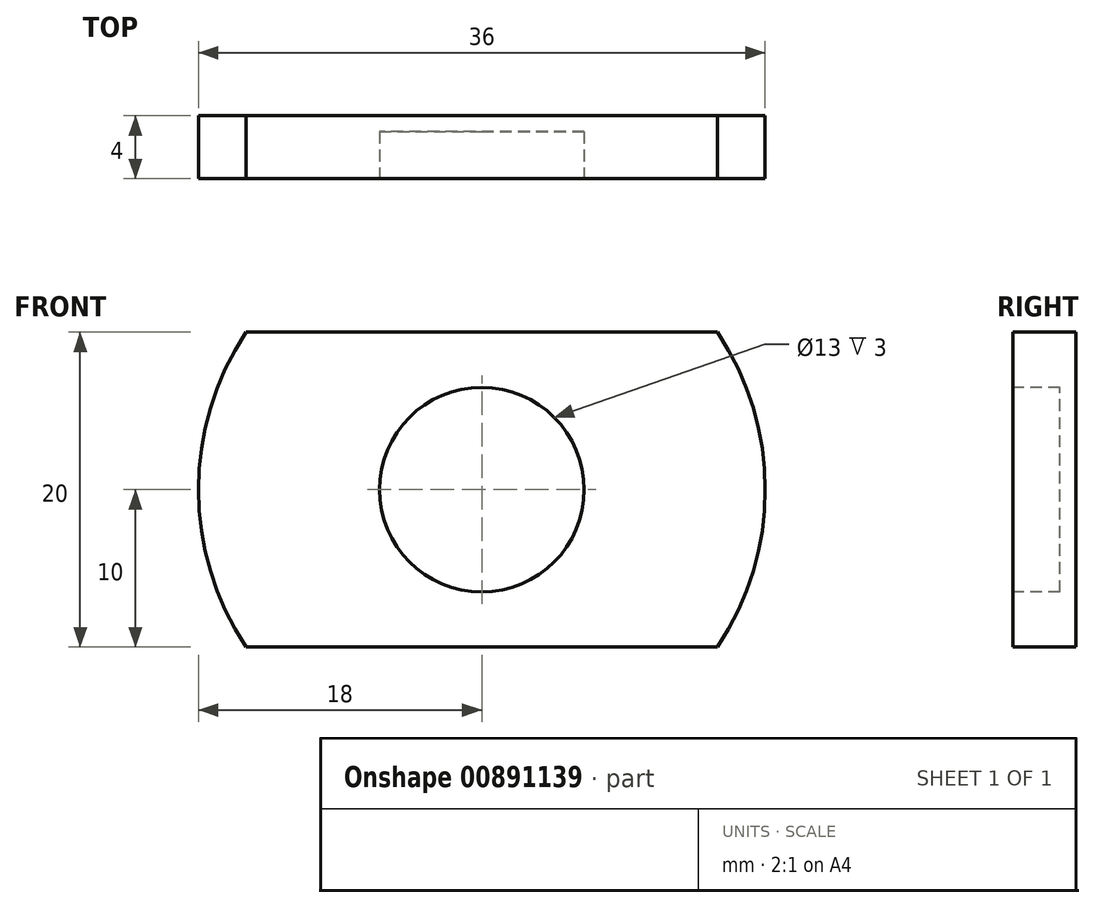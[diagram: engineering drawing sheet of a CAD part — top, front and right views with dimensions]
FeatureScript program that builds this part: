
annotation { "Feature Type Name" : "Feature", "Feature Type Description" : "" }
export const myFeature = defineFeature(function(context is Context, id is Id, definition is map)
    precondition{}
    {
        {
            var Q0;
            Q0=qCreatedBy(makeId("Front.planeOp"),FACE);
            var sketch = newSketch(context, id + "F0", { "sketchPlane" : qUnion([Q0])});
            skCircle(sketch, "E0", {"center": v(0, 0) * mm, "radius": 18 * mm});
            skSolve(sketch);
        }
        {
            var Q0;
            Q0=qSketchRegion(id+"F0",true);
            extrude(context, id + "F1", {"entities" : qUnion([Q0]), "endBound" : BoundingType.SYMMETRIC, "depth" : 4 * mm, "offsetDistance" : 25 * mm});
        }
        {
            var Q0;
            Q0=makeQuery(id+"F1.opExtrude","CAP_FACE",FACE,{"disambiguationData":[OSD([sQuery(id+"F0.wireOp",EDGE,"E0")])],"isStart":false});
            var sketch = newSketch(context, id + "F2", { "sketchPlane" : qUnion([Q0])});
            skCircle(sketch, "E1", {"center": v(0, 0) * mm, "radius": 6.5 * mm});
            skSolve(sketch);
        }
        {
            var Q0;
            Q0=qSketchRegion(id+"F2",true);
            extrude(context, id + "F3", {"entities" : qUnion([Q0]), "operationType" : NewBodyOperationType.REMOVE, "oppositeDirection" : true, "depth" : 3 * mm, "offsetDistance" : 25 * mm});
        }
        {
            var Q0;
            Q0=makeQuery(id+"F1.opExtrude","CAP_FACE",FACE,{"disambiguationData":[OSD([sQuery(id+"F0.wireOp",EDGE,"E0")])],"isStart":false});
            var sketch = newSketch(context, id + "F4", { "sketchPlane" : qUnion([Q0])});
            skLineSegment(sketch, "E2", {"start": v(18.82, 10) * mm, "end": v(-27.18, 10) * mm});
            skLineSegment(sketch, "E3", {"start": v(0, 0) * mm, "end": v(29.54, 0) * mm, "construction": true});
            skLineSegment(sketch, "E4.MirrorCS", {"start": v(18.82, -10) * mm, "end": v(-27.18, -10) * mm});
            skLineSegment(sketch, "E5", {"start": v(18.82, 10) * mm, "end": v(18.82, 18.28) * mm});
            skLineSegment(sketch, "E6", {"start": v(18.82, 18.28) * mm, "end": v(-27.18, 18.28) * mm});
            skLineSegment(sketch, "E7", {"start": v(-27.18, 18.28) * mm, "end": v(-27.18, 10) * mm});
            skLineSegment(sketch, "E8.MirrorCS", {"start": v(18.82, -18.28) * mm, "end": v(-27.18, -18.28) * mm});
            skLineSegment(sketch, "E9.MirrorCS", {"start": v(18.82, -10) * mm, "end": v(18.82, -18.28) * mm});
            skLineSegment(sketch, "E10.MirrorCS", {"start": v(-27.18, -18.28) * mm, "end": v(-27.18, -10) * mm});
            skSolve(sketch);
        }
        {
            var Q0;
            Q0 = qSketchRegion(id + "F4", true);
            extrude(context, id + "F5", {"entities" : qUnion([Q0]), "operationType" : NewBodyOperationType.REMOVE, "oppositeDirection" : true, "depth" : 25 * mm, "offsetDistance" : 25 * mm});
        }
    });
